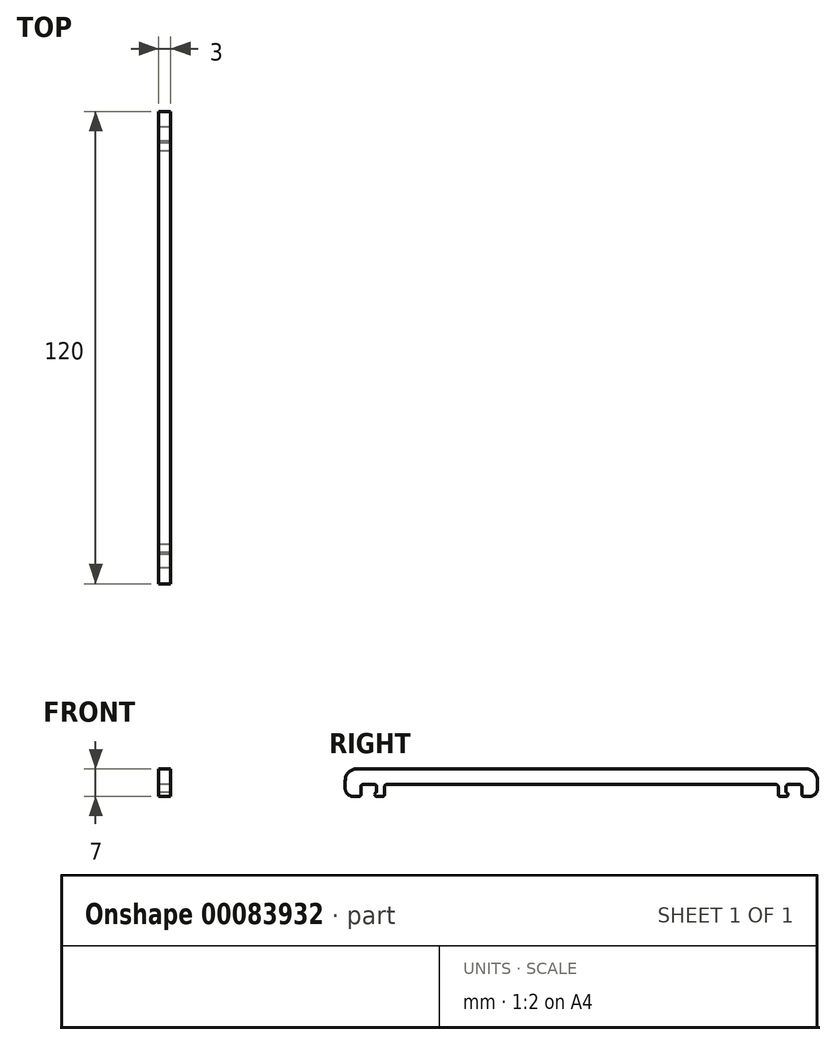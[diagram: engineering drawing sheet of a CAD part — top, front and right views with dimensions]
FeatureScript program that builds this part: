
annotation { "Feature Type Name" : "Feature", "Feature Type Description" : "" }
export const myFeature = defineFeature(function(context is Context, id is Id, definition is map)
    precondition{}
    {
        {
            var Q0;
            Q0=qCreatedBy(makeId("Right.planeOp"),FACE);
            var sketch = newSketch(context, id + "F0", { "sketchPlane" : qUnion([Q0])});
            skLineSegment(sketch, "E0.bottom", {"start": v(0, 0) * mm, "end": v(-60, 0) * mm});
            skLineSegment(sketch, "E0.top", {"start": v(0, 4) * mm, "end": v(-57, 4) * mm});
            skLineSegment(sketch, "E0.left", {"start": v(0, 0) * mm, "end": v(0, 4) * mm});
            skLineSegment(sketch, "E0.right", {"start": v(-60, 0) * mm, "end": v(-60, 1) * mm});
            skLineSegment(sketch, "E1.bottom", {"start": v(-60, 0) * mm, "end": v(-56, 0) * mm});
            skLineSegment(sketch, "E1.top", {"start": v(-58, -3) * mm, "end": v(-56.5, -3) * mm});
            skLineSegment(sketch, "E1.left", {"start": v(-60, 0) * mm, "end": v(-60, -1) * mm});
            skLineSegment(sketch, "E1.right", {"start": v(-56, 0) * mm, "end": v(-56, -2.5) * mm});
            skLineSegment(sketch, "E2.bottom", {"start": v(-52, 0) * mm, "end": v(-50, 0) * mm});
            skLineSegment(sketch, "E2.top", {"start": v(-52, -2) * mm, "end": v(-50, -2) * mm});
            skLineSegment(sketch, "E2.left", {"start": v(-52, 0) * mm, "end": v(-52, -2) * mm});
            skLineSegment(sketch, "E2.right", {"start": v(-50, 0) * mm, "end": v(-50, -2) * mm});
            skPoint(sketch, "E3.visualSharp", {"position": v(-60, -3) * mm});
            skArc(sketch, "E3.filletArc", {"start": v(-60, -1) * mm, "mid": v(-59.41, -2.41) * mm, "end": v(-58, -3) * mm});
            skLineSegment(sketch, "E4.top", {"start": v(-52, -3) * mm, "end": v(-50.5, -3) * mm});
            skLineSegment(sketch, "E4.left", {"start": v(-52, -2) * mm, "end": v(-52, -3) * mm});
            skLineSegment(sketch, "E4.right", {"start": v(-50, -2) * mm, "end": v(-50, -2.5) * mm});
            skArc(sketch, "E5", {"start": v(-52, -2) * mm, "mid": v(-52.5, -2.5) * mm, "end": v(-52, -3) * mm});
            skPoint(sketch, "E6.visualSharp", {"position": v(-56, -3) * mm});
            skArc(sketch, "E6.filletArc", {"start": v(-56.5, -3) * mm, "mid": v(-56.15, -2.85) * mm, "end": v(-56, -2.5) * mm});
            skPoint(sketch, "E7.visualSharp", {"position": v(-50, -3) * mm});
            skArc(sketch, "E7.filletArc", {"start": v(-50.5, -3) * mm, "mid": v(-50.15, -2.85) * mm, "end": v(-50, -2.5) * mm});
            skPoint(sketch, "E8.visualSharp", {"position": v(-60, 4) * mm});
            skArc(sketch, "E8.filletArc", {"start": v(-57, 4) * mm, "mid": v(-59.12, 3.12) * mm, "end": v(-60, 1) * mm});
            skSolve(sketch);
        }
        {
            var Q0;
            Q0 = qSketchRegion(id + "F0", true);
            extrude(context, id + "F1", {"entities" : qUnion([Q0]), "endBound" : BoundingType.SYMMETRIC, "depth" : 3 * mm});
        }
        {
            var Q0;
            Q0=makeQuery(id+"F1.opExtrude","SWEPT_EDGE",EDGE,{"disambiguationData":[OSD([sQuery(id+"F0.wireOp",EDGE,"E0.bottom"),sQuery(id+"F0.wireOp",EDGE,"E1.bottom"),sQuery(id+"F0.wireOp",EDGE,"E1.right")])]});
            var Q1;
            Q1=makeQuery(id+"F1.opExtrude","SWEPT_EDGE",EDGE,{"disambiguationData":[OSD([sQuery(id+"F0.wireOp",EDGE,"E0.bottom"),sQuery(id+"F0.wireOp",EDGE,"E2.bottom"),sQuery(id+"F0.wireOp",EDGE,"E2.left")])]});
            var Q2;
            Q2=makeQuery(id+"F1.opExtrude","SWEPT_EDGE",EDGE,{"disambiguationData":[OSD([sQuery(id+"F0.wireOp",EDGE,"E0.bottom"),sQuery(id+"F0.wireOp",EDGE,"E2.bottom"),sQuery(id+"F0.wireOp",EDGE,"E2.right")])]});
            fillet(context, id + "F2", {"entities" : qUnion([Q0, Q1, Q2]), "radius" : .5 * mm, "tangentPropagation" : true, "allowEdgeOverflow" : false});
        }
        {
            var Q0;
            Q0=makeQuery(id+"F1.opExtrude","SWEPT_BODY",BODY,{"disambiguationData":[OSD([sQuery(id+"F0.wireOp",EDGE,"E0.bottom"),sQuery(id+"F0.wireOp",EDGE,"E0.top"),sQuery(id+"F0.wireOp",EDGE,"E0.left"),sQuery(id+"F0.wireOp",EDGE,"E0.right"),sQuery(id+"F0.wireOp",EDGE,"E1.top"),sQuery(id+"F0.wireOp",EDGE,"E1.left"),sQuery(id+"F0.wireOp",EDGE,"E1.right"),sQuery(id+"F0.wireOp",EDGE,"E2.left"),sQuery(id+"F0.wireOp",EDGE,"E2.right"),sQuery(id+"F0.wireOp",EDGE,"E3.filletArc"),sQuery(id+"F0.wireOp",EDGE,"E4.top"),sQuery(id+"F0.wireOp",EDGE,"E4.right"),sQuery(id+"F0.wireOp",EDGE,"E5"),sQuery(id+"F0.wireOp",EDGE,"E6.filletArc"),sQuery(id+"F0.wireOp",EDGE,"E7.filletArc"),sQuery(id+"F0.wireOp",EDGE,"E8.filletArc")])]});
            var Q1;
            Q1=makeQuery(id+"F1.opExtrude","SWEPT_FACE",FACE,{"disambiguationData":[OSD([sQuery(id+"F0.wireOp",EDGE,"E0.left")])]});
            mirror(context, id + "F3", {"operationType" : NewBodyOperationType.ADD, "entities" : qUnion([Q0]), "mirrorPlane" : qUnion([Q1])});
        }
    });
